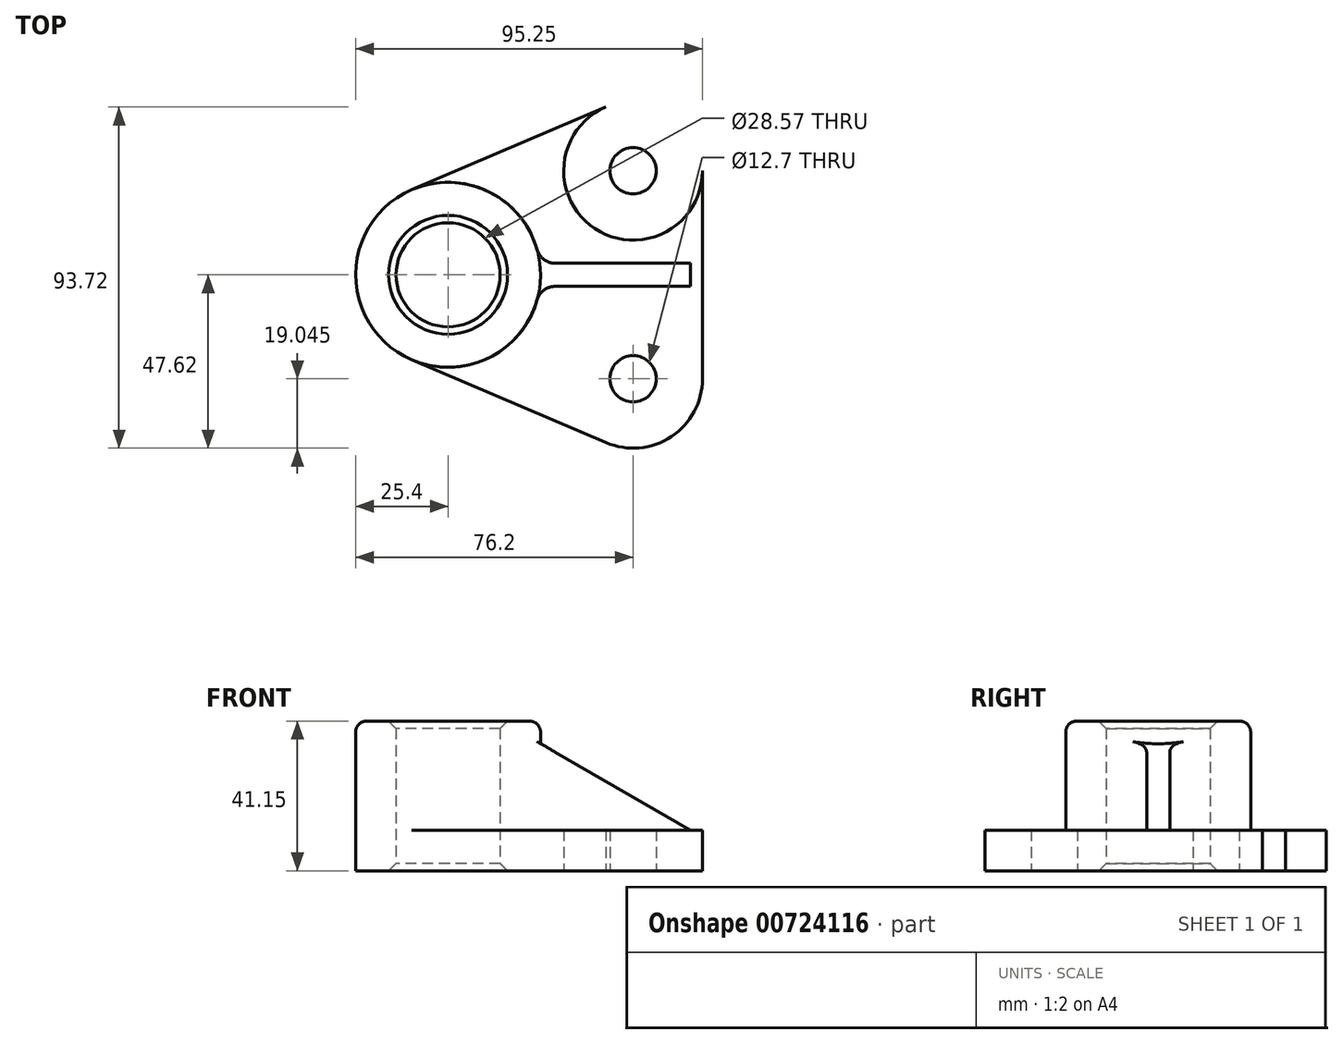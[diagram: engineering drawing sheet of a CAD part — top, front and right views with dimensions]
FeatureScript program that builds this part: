
annotation { "Feature Type Name" : "Feature", "Feature Type Description" : "" }
export const myFeature = defineFeature(function(context is Context, id is Id, definition is map)
    precondition{}
    {
        {
            var Q0;
            Q0=qCreatedBy(makeId("Top.planeOp"),FACE);
            var sketch = newSketch(context, id + "F0", { "sketchPlane" : qUnion([Q0])});
            skCircle(sketch, "E0", {"center": v(0, 0) * mm, "radius": 14.29 * mm});
            skCircle(sketch, "E1", {"center": v(0, 0) * mm, "radius": 25.4 * mm});
            skCircle(sketch, "E2", {"center": v(50.8, -28.58) * mm, "radius": 6.35 * mm});
            skLineSegment(sketch, "E3", {"start": v(0, 0) * mm, "end": v(0, -50.87) * mm, "construction": true});
            skLineSegment(sketch, "E4", {"start": v(0, 0) * mm, "end": v(84.62, 0) * mm, "construction": true});
            skCircle(sketch, "E5.MirrorC", {"center": v(50.8, 28.58) * mm, "radius": 6.35 * mm});
            skCircle(sketch, "E6", {"center": v(50.8, -28.58) * mm, "radius": 19.05 * mm});
            skCircle(sketch, "E7.MirrorC", {"center": v(50.8, 28.58) * mm, "radius": 19.05 * mm});
            skLineSegment(sketch, "E8", {"start": v(-9.97, -23.36) * mm, "end": v(43.33, -46.1) * mm});
            skLineSegment(sketch, "E9", {"start": v(-9.97, 23.36) * mm, "end": v(43.33, 46.1) * mm});
            skLineSegment(sketch, "E10", {"start": v(69.85, 28.58) * mm, "end": v(69.85, -28.58) * mm});
            skSolve(sketch);
        }
        {
            var Q0;
            Q0=makeQuery(id+"F0.imprint","IMPRINT",FACE,{"disambiguationData":[TD([[makeQuery(id+"F0.imprint","IMPRINT",EDGE,{"derivedFrom":sQuery(id+"F0.wireOp",EDGE,"E0")}),-1.0]])]});
            extrude(context, id + "F1", {"entities" : qUnion([Q0]), "depth" : 41.15 * mm, "offsetDistance" : 25.4 * mm});
        }
        {
            var Q0;
            {var subQ0=sQuery(id+"F0.wireOp",EDGE,"E8");Q0=makeQuery(id+"F0.imprint","IMPRINT",FACE,{"disambiguationData":[TD([[makeQuery(id+"F0.imprint","IMPRINT",EDGE,{"derivedFrom":subQ0}),1.0]])]});}
            var Q1;
            Q1=makeQuery(id+"F0.imprint","IMPRINT",FACE,{"disambiguationData":[TD([[makeQuery(id+"F0.imprint","IMPRINT",EDGE,{"derivedFrom":sQuery(id+"F0.wireOp",EDGE,"E5.MirrorC")}),1.0]])]});
            var Q2;
            Q2=makeQuery(id+"F0.imprint","IMPRINT",FACE,{"disambiguationData":[TD([[makeQuery(id+"F0.imprint","IMPRINT",EDGE,{"derivedFrom":sQuery(id+"F0.wireOp",EDGE,"E2")}),-1.0]])]});
            extrude(context, id + "F2", {"entities" : qUnion([Q0, Q1, Q2]), "operationType" : NewBodyOperationType.ADD, "depth" : 11.18 * mm, "offsetDistance" : 25.4 * mm});
        }
        {
            var Q0;
            Q0=makeQuery(id+"F1.opExtrude","CAP_EDGE",EDGE,{"disambiguationData":[OSD([sQuery(id+"F0.wireOp",EDGE,"E1")])],"isStart":false});
            fillet(context, id + "F3", {"entities" : qUnion([Q0]), "radius" : 3.05 * mm, "tangentPropagation" : true, "allowEdgeOverflow" : false});
        }
        {
            var Q0;
            Q0=makeQuery(id+"F1.opExtrude","CAP_EDGE",EDGE,{"disambiguationData":[OSD([sQuery(id+"F0.wireOp",EDGE,"E0")])],"isStart":false});
            var Q1;
            Q1=makeQuery(id+"F1.opExtrude","CAP_EDGE",EDGE,{"disambiguationData":[OSD([sQuery(id+"F0.wireOp",EDGE,"E0")])],"isStart":true});
            chamfer(context, id + "F4", {"entities" : qUnion([Q0, Q1]), "chamferType" : ChamferType.OFFSET_ANGLE, "width" : 2.03 * mm, "oppositeDirection" : false, "angle" : 45 * degree, "tangentPropagation" : true});
        }
        {
            var Q0;
            Q0=qCreatedBy(makeId("Front.planeOp"),FACE);
            var sketch = newSketch(context, id + "F5", { "sketchPlane" : qUnion([Q0])});
            skPoint(sketch, "E11", {"position": v(69.85, 0) * mm});
            skLineSegment(sketch, "E12", {"start": v(69.85, 0) * mm, "end": v(66.55, 0) * mm, "construction": true});
            skLineSegment(sketch, "E13", {"start": v(66.55, 0) * mm, "end": v(23.7, 0) * mm, "construction": true});
            skLineSegment(sketch, "E14", {"start": v(23.7, 0) * mm, "end": v(23.7, 11.18) * mm, "construction": true});
            skLineSegment(sketch, "E15", {"start": v(66.55, 0) * mm, "end": v(66.55, 11.18) * mm});
            skLineSegment(sketch, "E16", {"start": v(66.55, 11.18) * mm, "end": v(23.7, 11.18) * mm});
            skLineSegment(sketch, "E17", {"start": v(66.55, 11.18) * mm, "end": v(23.7, 35.92) * mm});
            skLineSegment(sketch, "E18", {"start": v(23.7, 11.18) * mm, "end": v(23.7, 35.92) * mm});
            skSolve(sketch);
        }
        {
            var Q0;
            Q0=makeQuery(id+"F5.imprint","IMPRINT",FACE,{"disambiguationData":[TD([[makeQuery(id+"F5.imprint","IMPRINT",EDGE,{"derivedFrom":sQuery(id+"F5.wireOp",EDGE,"E16")}),-1.0]])]});
            extrude(context, id + "F6", {"entities" : qUnion([Q0]), "operationType" : NewBodyOperationType.ADD, "endBound" : BoundingType.SYMMETRIC, "depth" : 6.35 * mm, "offsetDistance" : 25.4 * mm});
        }
        {
            var Q0;
            Q0=makeQuery(id+"F6.opExtrude","CAP_EDGE",EDGE,{"disambiguationData":[OSD([sQuery(id+"F5.wireOp",EDGE,"E16")])],"isStart":false});
            var Q1;
            Q1=makeQuery(id+"F6.opExtrude","CAP_EDGE",EDGE,{"disambiguationData":[OSD([sQuery(id+"F5.wireOp",EDGE,"E16")])],"isStart":true});
            var Q2;
            {var subQ0=sQuery(id+"F0.wireOp",EDGE,"E1");var subQ1=sQuery(id+"F0.wireOp",EDGE,"E8");Q2=makeQuery(id+"F6.boolean.opBoolean","SPLIT",EDGE,{"disambiguationData":[TD([makeQuery(id+"F2.opExtrude","SWEPT_FACE",FACE,{"disambiguationData":[OSD([subQ1])]})])],"derivedFrom":makeQuery(id+"F2.opExtrude","CAP_EDGE",EDGE,{"disambiguationData":[OSD([subQ0])],"isStart":false})});}
            var Q3;
            {var subQ0=sQuery(id+"F0.wireOp",EDGE,"E1");var subQ1=sQuery(id+"F0.wireOp",EDGE,"E9");Q3=makeQuery(id+"F6.boolean.opBoolean","SPLIT",EDGE,{"disambiguationData":[TD([makeQuery(id+"F2.opExtrude","SWEPT_FACE",FACE,{"disambiguationData":[OSD([subQ1])]})])],"derivedFrom":makeQuery(id+"F2.opExtrude","CAP_EDGE",EDGE,{"disambiguationData":[OSD([subQ0])],"isStart":false})});}
            var Q4;
            Q4=makeQuery(id+"F6.boolean.opBoolean","INTERSECT",EDGE,{"derivedFrom":[makeQuery(id+"F1.opExtrude","SWEPT_FACE",FACE,{"disambiguationData":[OSD([sQuery(id+"F0.wireOp",EDGE,"E1")])]}),makeQuery(id+"F6.opExtrude","CAP_FACE",FACE,{"disambiguationData":[OSD([sQuery(id+"F5.wireOp",EDGE,"E16"),sQuery(id+"F5.wireOp",EDGE,"E17"),sQuery(id+"F5.wireOp",EDGE,"E18")])],"isStart":false})]});
            var Q5;
            Q5=makeQuery(id+"F6.boolean.opBoolean","INTERSECT",EDGE,{"derivedFrom":[makeQuery(id+"F1.opExtrude","SWEPT_FACE",FACE,{"disambiguationData":[OSD([sQuery(id+"F0.wireOp",EDGE,"E1")])]}),makeQuery(id+"F6.opExtrude","CAP_FACE",FACE,{"disambiguationData":[OSD([sQuery(id+"F5.wireOp",EDGE,"E16"),sQuery(id+"F5.wireOp",EDGE,"E17"),sQuery(id+"F5.wireOp",EDGE,"E18")])],"isStart":true})]});
            fillet(context, id + "F7", {"entities" : qUnion([Q0, Q1, Q2, Q3, Q4, Q5]), "radius" : 5.08 * mm, "tangentPropagation" : true, "allowEdgeOverflow" : false});
        }
    });
